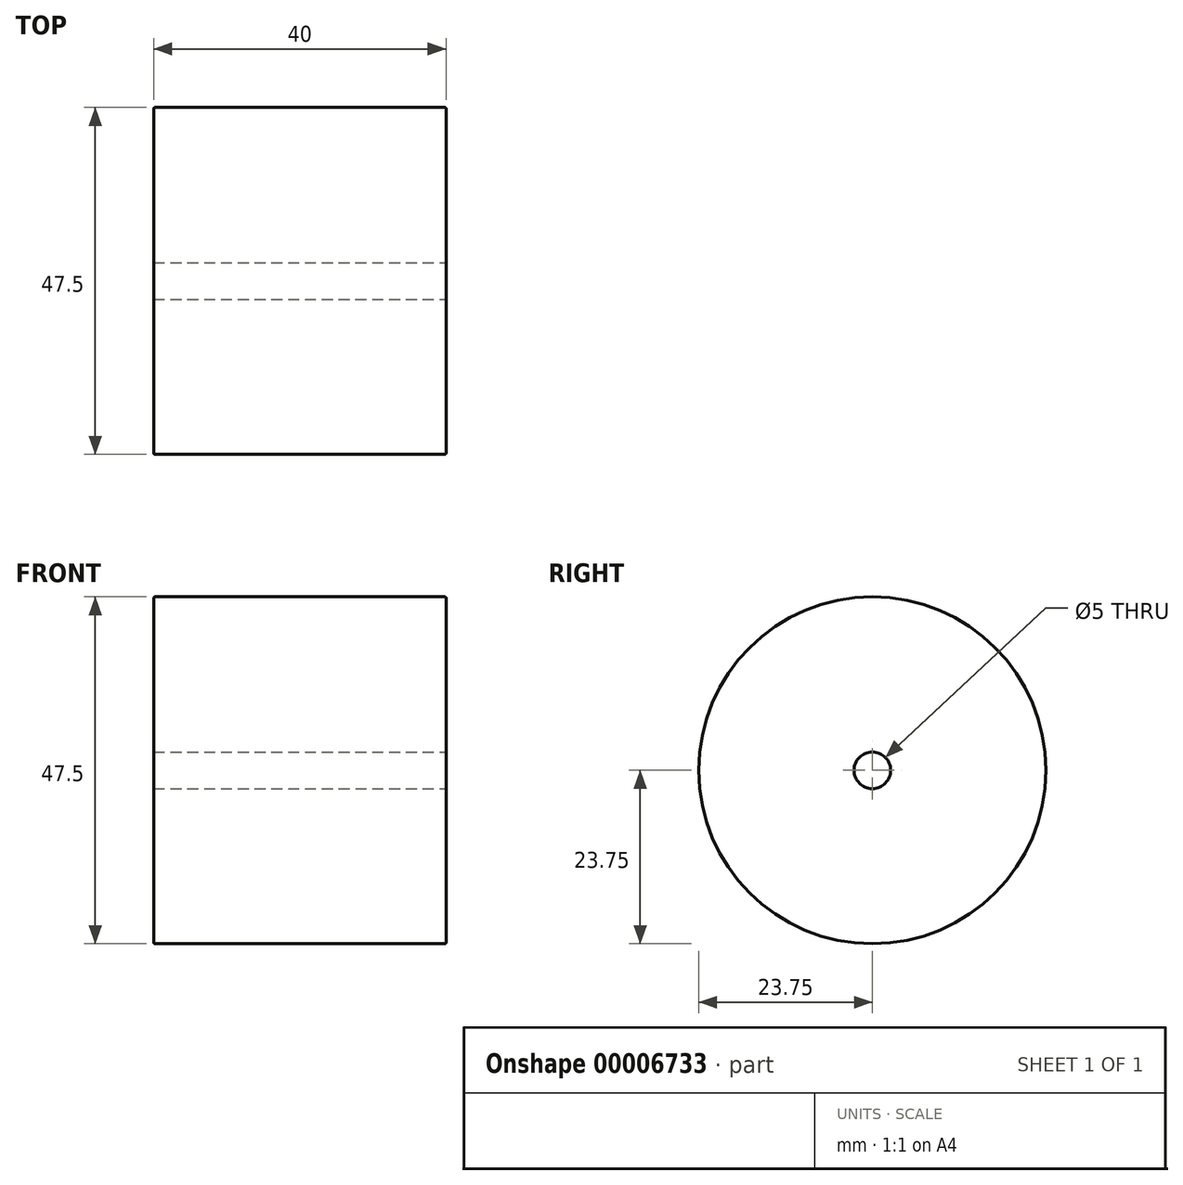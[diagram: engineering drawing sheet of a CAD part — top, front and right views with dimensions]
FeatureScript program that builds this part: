
annotation { "Feature Type Name" : "Feature", "Feature Type Description" : "" }
export const myFeature = defineFeature(function(context is Context, id is Id, definition is map)
    precondition{}
    {
        {
            var Q0;
            Q0=qCreatedBy(makeId("Right.planeOp"),FACE);
            var sketch = newSketch(context, id + "F0", { "sketchPlane" : qUnion([Q0])});
            skCircle(sketch, "E0", {"center": v(0, 0) * mm, "radius": 23.75 * mm});
            skSolve(sketch);
        }
        {
            var Q0;
            Q0=makeQuery(id+"F0.imprint","IMPRINT",FACE,{"disambiguationData":[TD([[makeQuery(id+"F0.imprint","IMPRINT",EDGE,{"derivedFrom":sQuery(id+"F0.wireOp",EDGE,"E0")}),1.0]])]});
            extrude(context, id + "F1", {"entities" : qUnion([Q0]), "endBound" : BoundingType.SYMMETRIC, "depth" : 40 * mm});
        }
        {
            var Q0;
            Q0=makeQuery(id+"F1.opExtrude","CAP_FACE",FACE,{"disambiguationData":[OSD([sQuery(id+"F0.wireOp",EDGE,"E0")])],"isStart":false});
            var sketch = newSketch(context, id + "F2", { "sketchPlane" : qUnion([Q0])});
            skCircle(sketch, "E1", {"center": v(0, 0) * mm, "radius": 2.5 * mm});
            skSolve(sketch);
        }
        {
            var Q0;
            Q0 = qSketchRegion(id + "F2", true);
            extrude(context, id + "F3", {"entities" : qUnion([Q0]), "operationType" : NewBodyOperationType.REMOVE, "endBound" : BoundingType.THROUGH_ALL, "oppositeDirection" : true, "depth" : 25 * mm});
        }
        {
            var Q0;
            Q0=makeQuery(id+"F1.opExtrude","CAP_EDGE",EDGE,{"disambiguationData":[OSD([sQuery(id+"F0.wireOp",EDGE,"E0")])],"isStart":false});
            var Q1;
            Q1=makeQuery(id+"F1.opExtrude","CAP_EDGE",EDGE,{"disambiguationData":[OSD([sQuery(id+"F0.wireOp",EDGE,"E0")])],"isStart":true});
            fillet(context, id + "F4", {"entities" : qUnion([Q0, Q1]), "radius" : 0.2 * mm, "tangentPropagation" : true, "allowEdgeOverflow" : false});
        }
    });
